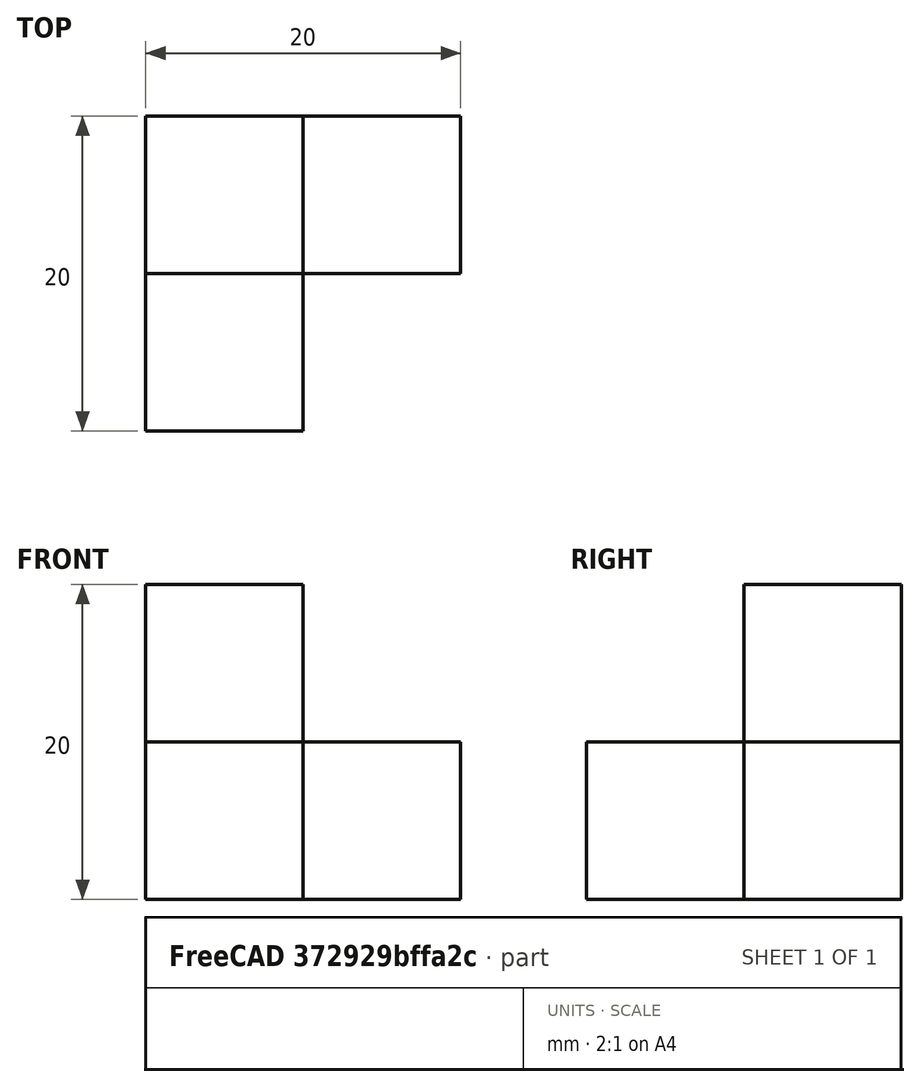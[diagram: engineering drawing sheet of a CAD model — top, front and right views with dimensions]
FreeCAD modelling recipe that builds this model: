
FCSTD DOCUMENT  (FreeCAD 1.0R39319 (Git))
Label: ojt1_t05r01_refine shapes
License: All rights reserved
LicenseURL: https://en.wikipedia.org/wiki/All_rights_reserved
objects: Part::Box×4, Part::MultiFuse×1
note: 5 computed .brp shape members not serialized (recipe doc carries the construction recipe); baked Part::Feature solids carry a one-line shape summary decoded from their .brp

FEATURE [Part::Box] Box  label="Cube"
  AttacherType = Attacher::AttachEngine3D
  Height = 10
  Length = 10
  Width = 10
FEATURE [Part::Box] Box001  label="Cube001"
  AttacherType = Attacher::AttachEngine3D
  Height = 10
  Length = 10
  Placement = pos=(0,0,10) rot=(0,0,1;0rad)
  Width = 10
FEATURE [Part::Box] Box002  label="Cube002"
  AttacherType = Attacher::AttachEngine3D
  Height = 10
  Length = 10
  Placement = pos=(10,0,0) rot=(0,0,1;0rad)
  Width = 10
FEATURE [Part::Box] Box003  label="Cube003"
  AttacherType = Attacher::AttachEngine3D
  Height = 10
  Length = 10
  Placement = pos=(0,-10,0) rot=(0,0,1;0rad)
  Width = 10
FEATURE [Part::MultiFuse] Fusion
  Refine = true
  Shapes = -> [Box,Box001,Box002,Box003]
